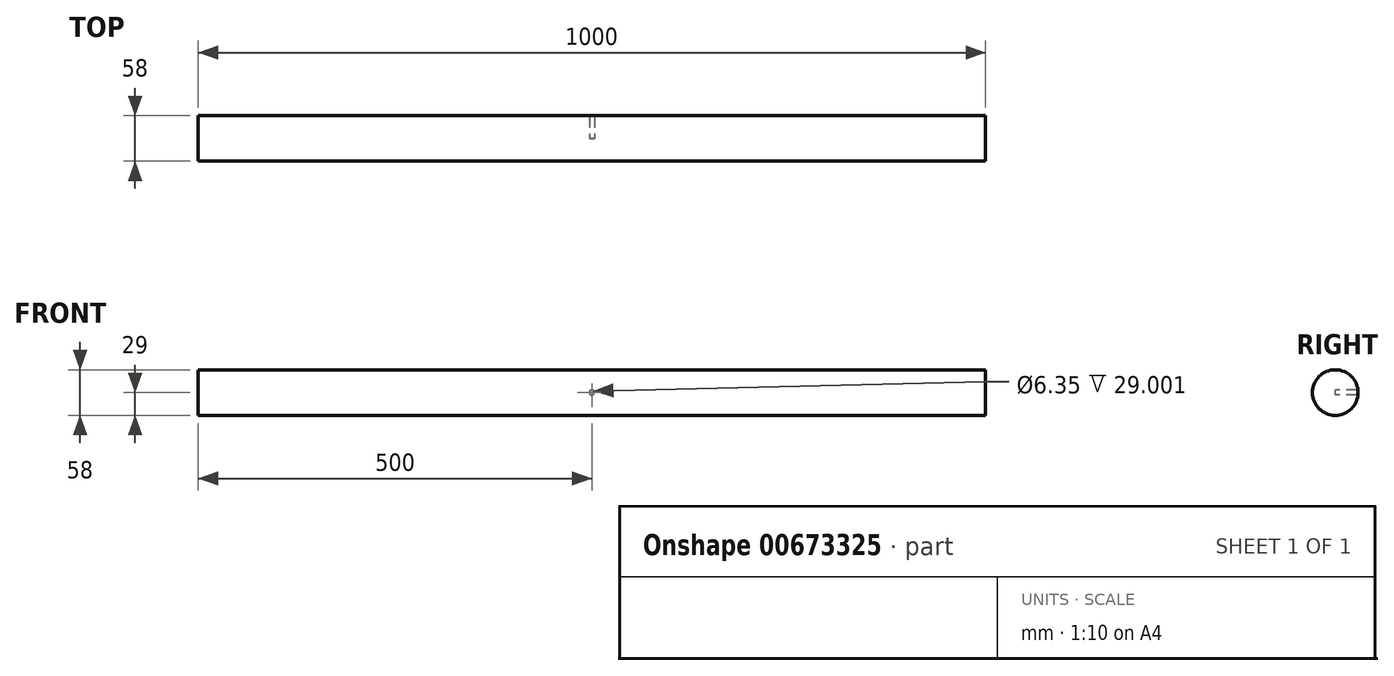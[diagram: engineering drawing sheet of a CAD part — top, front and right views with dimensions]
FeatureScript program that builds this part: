
annotation { "Feature Type Name" : "Feature", "Feature Type Description" : "" }
export const myFeature = defineFeature(function(context is Context, id is Id, definition is map)
    precondition{}
    {
        {
            var Q0;
            Q0=qCreatedBy(makeId("Front.planeOp"),FACE);
            var sketch = newSketch(context, id + "F0", { "sketchPlane" : qUnion([Q0])});
            skLineSegment(sketch, "E0", {"start": v(0, 0) * mm, "end": v(1000, 0) * mm});
            skSolve(sketch);
        }
        {
            var Q0;
            Q0=qCreatedBy(makeId("Right.planeOp"),FACE);
            var sketch = newSketch(context, id + "F1", { "sketchPlane" : qUnion([Q0])});
            skCircle(sketch, "E1", {"center": v(0, 0) * mm, "radius": 29 * mm});
            skSolve(sketch);
        }
        {
            var Q0;
            Q0=makeQuery(id+"F1.imprint","IMPRINT",FACE,{"disambiguationData":[TD([[makeQuery(id+"F1.imprint","IMPRINT",EDGE,{"derivedFrom":sQuery(id+"F1.wireOp",EDGE,"E1")}),1.0]])]});
            var Q1;
            Q1=sQuery(id+"F0.wireOp",EDGE,"E0");
            sweep(context, id + "F2", {"profiles" : qUnion([Q0]), "path" : qUnion([Q1])});
        }
        {
            var Q0;
            Q0=qCreatedBy(makeId("Front.planeOp"),FACE);
            var sketch = newSketch(context, id + "F3", { "sketchPlane" : qUnion([Q0])});
            skCircle(sketch, "E2", {"center": v(500, 0) * mm, "radius": 3.91 * mm});
            skSolve(sketch);
        }
        {
            var Q0;
            Q0=sQuery(id+"F3.wireOp",VERTEX,"E2.center");
            var Q1;
            Q1=makeQuery(id+"F2.opSweep","SWEPT_BODY",BODY,{"disambiguationData":[OSD([sQuery(id+"F0.wireOp",EDGE,"E0"),sQuery(id+"F1.wireOp",EDGE,"E1")])]});
            hole(context, id + "F4", {"style" : HoleStyle.SIMPLE, "endStyle" : HoleEndStyle.THROUGH, "holeDiameter" : 6.35 * mm, "majorDiameter" : 6.35 * mm, "isTappedThrough" : true, "tappedDepth" : 12.7 * mm, "tapClearance" : 3, "locations" : qUnion([Q0]), "scope" : qUnion([Q1])});
        }
    });
